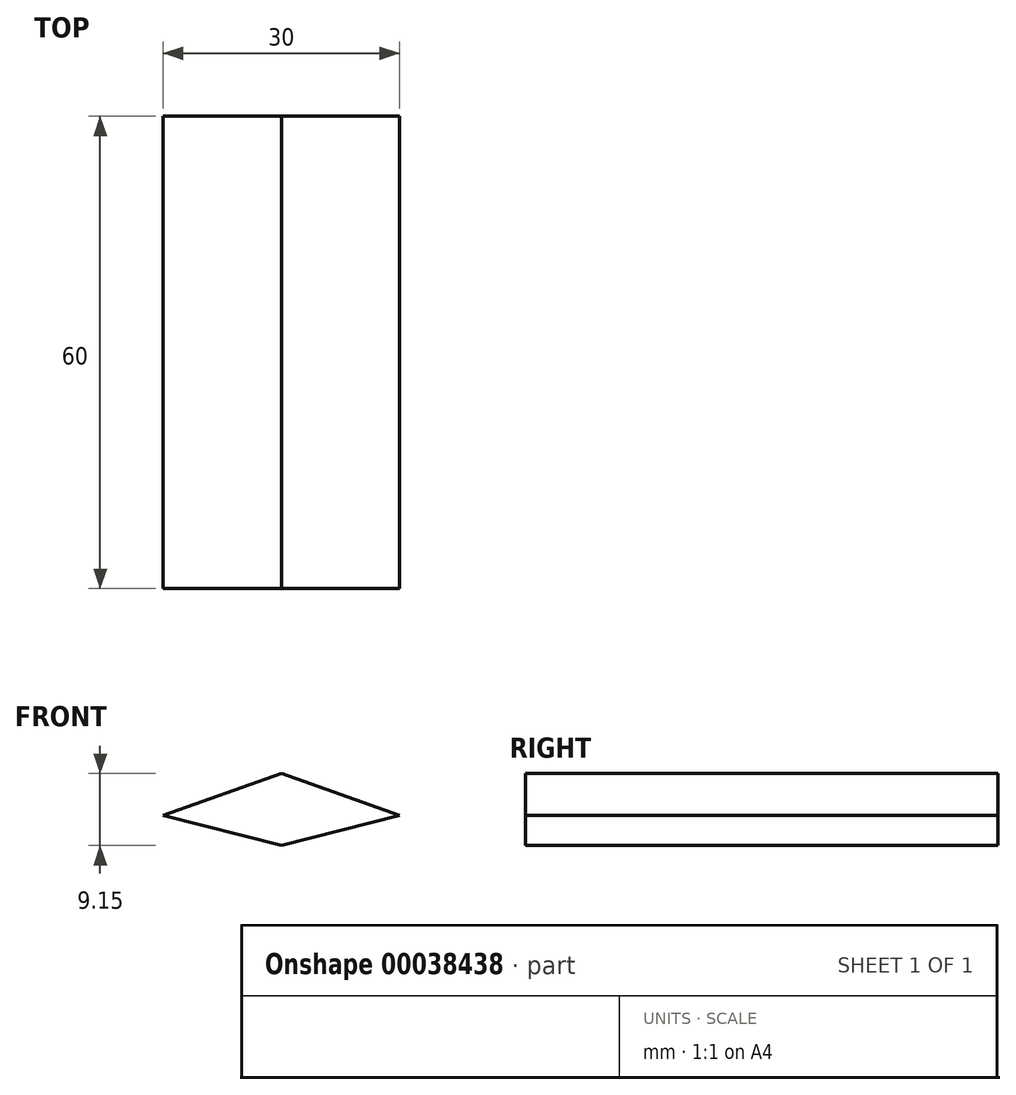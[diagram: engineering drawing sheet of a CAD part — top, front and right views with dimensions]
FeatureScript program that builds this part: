
annotation { "Feature Type Name" : "Feature", "Feature Type Description" : "" }
export const myFeature = defineFeature(function(context is Context, id is Id, definition is map)
    precondition{}
    {
        {
            var Q0;
            Q0=qCreatedBy(makeId("Front.planeOp"),FACE);
            var sketch = newSketch(context, id + "F0", { "sketchPlane" : qUnion([Q0])});
            skLineSegment(sketch, "E0", {"start": v(0, 0) * mm, "end": v(-15, 3.81) * mm});
            skLineSegment(sketch, "E1", {"start": v(-15, 3.81) * mm, "end": v(0, 9.15) * mm});
            skLineSegment(sketch, "E2", {"start": v(0, 9.15) * mm, "end": v(0, 0) * mm});
            skLineSegment(sketch, "E3", {"start": v(0, 9.15) * mm, "end": v(15, 3.8) * mm});
            skLineSegment(sketch, "E4", {"start": v(15, 3.81) * mm, "end": v(0, 0) * mm});
            skSolve(sketch);
        }
        {
            var Q0;
            Q0=makeQuery(id+"F0.imprint","IMPRINT",FACE,{"disambiguationData":[TD([[makeQuery(id+"F0.imprint","IMPRINT",EDGE,{"derivedFrom":sQuery(id+"F0.wireOp",EDGE,"E0")}),-1.0]])]});
            var Q1;
            Q1=makeQuery(id+"F0.imprint","IMPRINT",FACE,{"disambiguationData":[TD([[makeQuery(id+"F0.imprint","IMPRINT",EDGE,{"derivedFrom":sQuery(id+"F0.wireOp",EDGE,"E2")}),1.0]])]});
            extrude(context, id + "F1", {"entities" : qUnion([Q0, Q1]), "depth" : 60 * mm});
        }
    });
